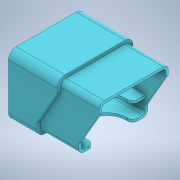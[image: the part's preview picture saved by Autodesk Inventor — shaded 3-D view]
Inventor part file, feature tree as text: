
AUTODESK INVENTOR PART (.ipt)
format: ipt  version: 2020 (Build 240168000, 168)  size: 337,920 bytes
history: native  units: in
note: dims shown in document units (in); Inventor stores cm internally (conversion verified against a paired STEP export)
features: extrude x7, fillet x5, sketch x3, other x2, chamfer x1, mirror x1
ambient origin geometry x8: Origin, YZ Plane, XZ Plane, XY Plane, X Axis, Y Axis, Z Axis, Center Point
bodies: Solid1 (feature_tree)
feature tree (19):
  other  "ESP32 Feather.ipt"
  sketch  "Sketch3"  dims[d1=0.3937in d2=0.0394in]
  extrude  "Extrusion1"  Depth=0.0394in
  extrude  "Extrusion2"  Depth=0.0394in
  extrude  "Extrusion3"  Depth=0.0787in
  fillet  "Fillet1"  Radius=0.1969in
  fillet  "Fillet2"  Radius=0.1969in
  fillet  "Fillet3"  Radius=0.2067in
  sketch  "Sketch4"  dims[d3=0.0591in d4=0.0394in]
  extrude  "Extrusion4"  Depth=0.9843in
  extrude  "Extrusion5"  Depth=0.0787in
  extrude  "Extrusion6"  Depth=0.0394in
  chamfer  "Chamfer1"  Distance=0.0394in
  fillet  "Fillet6"  Radius=0.0394in
  extrude  "Extrusion8"  Depth=0.0787in
  fillet  "Fillet7"  Radius=0.0098in
  mirror  "Mirror2"
  other  "ESP32 Feather"
  sketch  "Sketch6"  dims[d7=0.0394in d8=0.0197in d9=0.0098in d13=0.1969in d14=0.1969in d17=0.2067in d18=0.9843in d19=0.5118in d21=0.0394in d22=0.0394in d23=0.0394in d24=0.0098in d25=0.0098in d26=0.0098in d27=0.0098in d28=0.0098in d29=0.0098in d30=0.5906in d32=30.0deg d33=0.5906in d35=0.0098in d36=0.1969in d37=0.1969in d38=0.4872in d39=0.0in d40=0.0886in d41=0.0in d42=0.0394in d43=0.0in d44=0.0394in d45=0.0787in d46=0.1181in d50=45.0deg d52=0.1969in d53=0.0591in d54=45.0deg d55=0.0394in d56=0.0394in d57=0.0in d58=0.0374in d59=0.0in d60=0.0689in d61=0.0in d62=0.0374in d63=0.0591in d64=45.0deg d65=0.0591in d66=0.0394in d67=1.4567in d70=0.1969in d71=0.0984in d72=45.0deg d80=0.3937in d81=0.2953in d82=0.3937in d83=0.0in d84=0.0787in]
